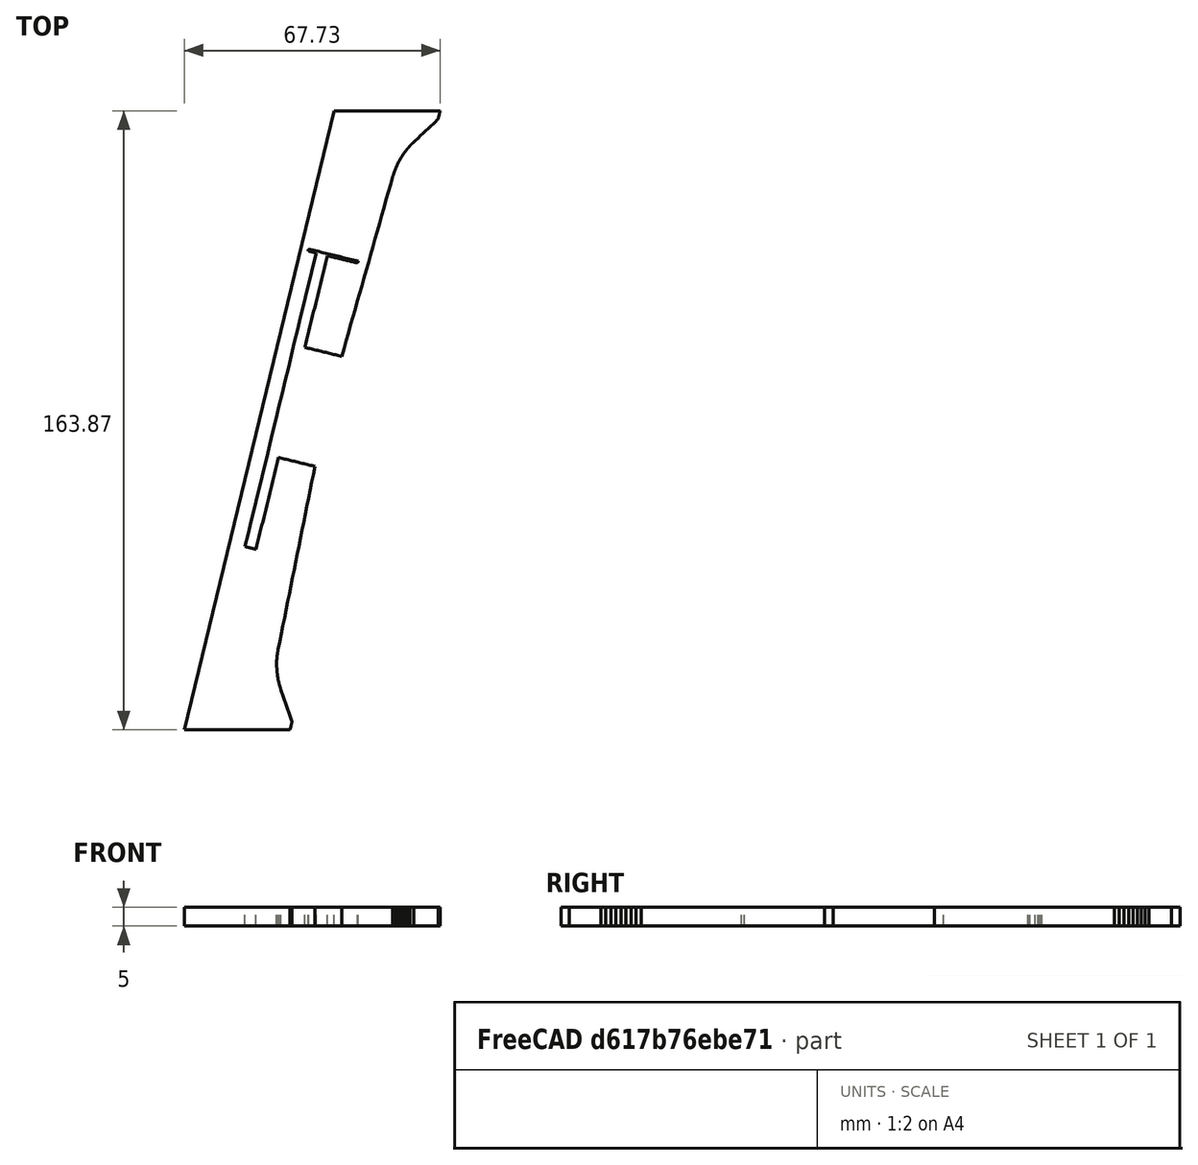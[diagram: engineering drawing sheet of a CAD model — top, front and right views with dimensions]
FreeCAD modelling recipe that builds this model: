
FCSTD DOCUMENT  (FreeCAD 0.19R)
Label: F-35_v2_parts_2
License: All rights reserved
LicenseURL: http://en.wikipedia.org/wiki/All_rights_reserved
objects: App::DocumentObjectGroup×2, PartDesign::CoordinateSystem×2, Sketcher::SketchObject×1, PartDesign::Pad×1, PartDesign::Body×1, App::FeaturePython×1, App::Part×1
note: 6 computed .brp shape members not serialized (recipe doc carries the construction recipe); baked Part::Feature solids carry a one-line shape summary decoded from their .brp

FEATURE [App::DocumentObjectGroup] Parts
FEATURE [PartDesign::CoordinateSystem] LCS_Origin
  AttacherType = Attacher::AttachEngine3D
  MapMode = 2
  Support = -> [X_Axis]
FEATURE [App::DocumentObjectGroup] Constraints
FEATURE [Sketcher::SketchObject] Sketch007
  FullyConstrained = false
  sketch-geometry (36):
    g0: BSplineCurve PolesCount=2 KnotsCount=2 Degree=1 IsPeriodic=0
    g1: BSplineCurve PolesCount=2 KnotsCount=2 Degree=1 IsPeriodic=0
    g2: BSplineCurve PolesCount=2 KnotsCount=2 Degree=1 IsPeriodic=0
    g3: BSplineCurve PolesCount=2 KnotsCount=2 Degree=1 IsPeriodic=0
    g4: BSplineCurve PolesCount=2 KnotsCount=2 Degree=1 IsPeriodic=0
    g5: BSplineCurve PolesCount=2 KnotsCount=2 Degree=1 IsPeriodic=0
    g6: BSplineCurve PolesCount=2 KnotsCount=2 Degree=1 IsPeriodic=0
    g7: BSplineCurve PolesCount=2 KnotsCount=2 Degree=1 IsPeriodic=0
    g8: BSplineCurve PolesCount=2 KnotsCount=2 Degree=1 IsPeriodic=0
    g9: BSplineCurve PolesCount=2 KnotsCount=2 Degree=1 IsPeriodic=0
    g10: BSplineCurve PolesCount=2 KnotsCount=2 Degree=1 IsPeriodic=0
    g11: BSplineCurve PolesCount=2 KnotsCount=2 Degree=1 IsPeriodic=0
    g12: BSplineCurve PolesCount=2 KnotsCount=2 Degree=1 IsPeriodic=0
    g13: BSplineCurve PolesCount=2 KnotsCount=2 Degree=1 IsPeriodic=0
    g14: BSplineCurve PolesCount=2 KnotsCount=2 Degree=1 IsPeriodic=0
    g15: BSplineCurve PolesCount=2 KnotsCount=2 Degree=1 IsPeriodic=0
    g16: BSplineCurve PolesCount=2 KnotsCount=2 Degree=1 IsPeriodic=0
    g17: BSplineCurve PolesCount=2 KnotsCount=2 Degree=1 IsPeriodic=0
    g18: BSplineCurve PolesCount=2 KnotsCount=2 Degree=1 IsPeriodic=0
    g19: BSplineCurve PolesCount=2 KnotsCount=2 Degree=1 IsPeriodic=0
    g20: BSplineCurve PolesCount=2 KnotsCount=2 Degree=1 IsPeriodic=0
    g21: BSplineCurve PolesCount=2 KnotsCount=2 Degree=1 IsPeriodic=0
    g22: BSplineCurve PolesCount=2 KnotsCount=2 Degree=1 IsPeriodic=0
    g23: BSplineCurve PolesCount=2 KnotsCount=2 Degree=1 IsPeriodic=0
    g24: BSplineCurve PolesCount=2 KnotsCount=2 Degree=1 IsPeriodic=0
    g25: BSplineCurve PolesCount=2 KnotsCount=2 Degree=1 IsPeriodic=0
    g26: BSplineCurve PolesCount=2 KnotsCount=2 Degree=1 IsPeriodic=0
    g27: BSplineCurve PolesCount=2 KnotsCount=2 Degree=1 IsPeriodic=0
    g28: BSplineCurve PolesCount=2 KnotsCount=2 Degree=1 IsPeriodic=0
    g29: BSplineCurve PolesCount=2 KnotsCount=2 Degree=1 IsPeriodic=0
    g30: BSplineCurve PolesCount=2 KnotsCount=2 Degree=1 IsPeriodic=0
    g31: BSplineCurve PolesCount=2 KnotsCount=2 Degree=1 IsPeriodic=0
    g32: BSplineCurve PolesCount=2 KnotsCount=2 Degree=1 IsPeriodic=0
    g33: BSplineCurve PolesCount=2 KnotsCount=2 Degree=1 IsPeriodic=0
    g34: BSplineCurve PolesCount=2 KnotsCount=2 Degree=1 IsPeriodic=0
    g35: LineSegment StartX=706.521 StartY=-379.006 StartZ=0 EndX=746.243 EndY=-215.14 EndZ=0
  constraints (16):
    c: Coincident(g11,g12)
    c: Coincident(g12,g13)
    c: Coincident(g13,g14)
    c: Coincident(g14,g15)
    c: Coincident(g15,g16)
    c: Coincident(g16,g17)
    c: Coincident(g17,g18)
    c: Coincident(g27,g28)
    c: Coincident(g28,g29)
    c: Coincident(g29,g30)
    c: Coincident(g30,g31)
    c: Coincident(g31,g32)
    c: Coincident(g32,g33)
    c: Coincident(g33,g34)
    c: Coincident(g8,g35)
    c: Coincident(g7,g35)
FEATURE [PartDesign::Pad] Pad007
  Direction = (1,1,1)
  Length = 5
  Length2 = 100
  Profile = -> Sketch007
  Type = 0
FEATURE [PartDesign::Body] Body007  label="Part2"
  Group = -> [Sketch007,Pad007]
  Origin = -> Origin008
  Tip = -> Pad007
FEATURE [App::FeaturePython] Variables001  label="Variables"  # WARN: FeaturePython — macro-defined, semantics opaque (R4)
FEATURE [PartDesign::CoordinateSystem] LCS_1
  AttacherType = Attacher::AttachEngine3D
  AttachmentOffset = pos=(0,0,-168.611) rot=(0,0,1;0rad)
  MapMode = 7
  Placement = pos=(746.243,-215.141,5) rot=(0.986024,-0.117806,-0.117806;1.58487rad)
  Support = -> [Pad007]
FEATURE [App::Part] Model
  Configuration = 0
  Group = -> [LCS_Origin,Constraints,Body007,Variables001,LCS_1]
  Origin = -> Origin
  Type = Assembly4 Model
